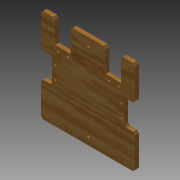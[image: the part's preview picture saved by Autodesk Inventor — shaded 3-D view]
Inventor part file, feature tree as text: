
AUTODESK INVENTOR PART (.ipt)
format: ipt  version: 2013 (Build 170138000, 138)  size: 198,656 bytes
history: native  units: in
note: dims shown in document units (in); Inventor stores cm internally (conversion verified against a paired STEP export)
features: sketch x3, chamfer x2, hole x2, extrude x1
ambient origin geometry x8: Origin, YZ Plane, XZ Plane, XY Plane, X Axis, Y Axis, Z Axis, Center Point
bodies: Solid1 (feature_tree)
feature tree (8):
  extrude  "Extrusion1"  Depth=6.0in
  chamfer  "Chamfer1"  Distance=0.6875in
  chamfer  "Chamfer2"  Distance=1.625in
  hole  "Hole1"  [1 undecoded]
  hole  "Hole2"  [1 undecoded]
  sketch  "Sketch1"  dims[d0=6.0in d1=6.0in]
  sketch  "Sketch2"  dims[d2=1.625in]
  sketch  "Sketch3"  dims[d3=2.1875in d4=0.6875in d5=1.625in d6=0.6875in d7=2.1875in d8=6.0in d9=2.1875in d10=0.1695in d11=0.1695in d12=0.1695in d13=0.1695in d15=0.875in d16=0.875in d17=0.875in d18=0.875in d19=0.4in d20=0.4in d21=0.4in d22=0.4in d23=0.25in d24=0.0in d25=0.125in d26=0.125in d27=45.0deg d28=4.23in d29=1.0in d30=1.0in d31=0.885in d32=1.5in d33=0.125in d34=0.125in d35=45.0deg d37=0.625in d39=0.625in d40=0.1875in d41=0.1875in d42=0.25in d43=0.1695in d44=0.75in d45=0.375in d46=0.25in d47=0.5635in d48=1.0in d49=0.8108in d50=3.0in d51=3.0in d52=0.5in d53=0.5in d54=0.177in d55=0.75in d56=0.375in d57=0.25in d58=0.5635in d59=1.0in d60=0.8108in]
note: 2 required parameter values undecoded (feature->parameter linkage not recoverable at this tier; creation-order binding heuristic only, values carry confidence <= 0.55)
